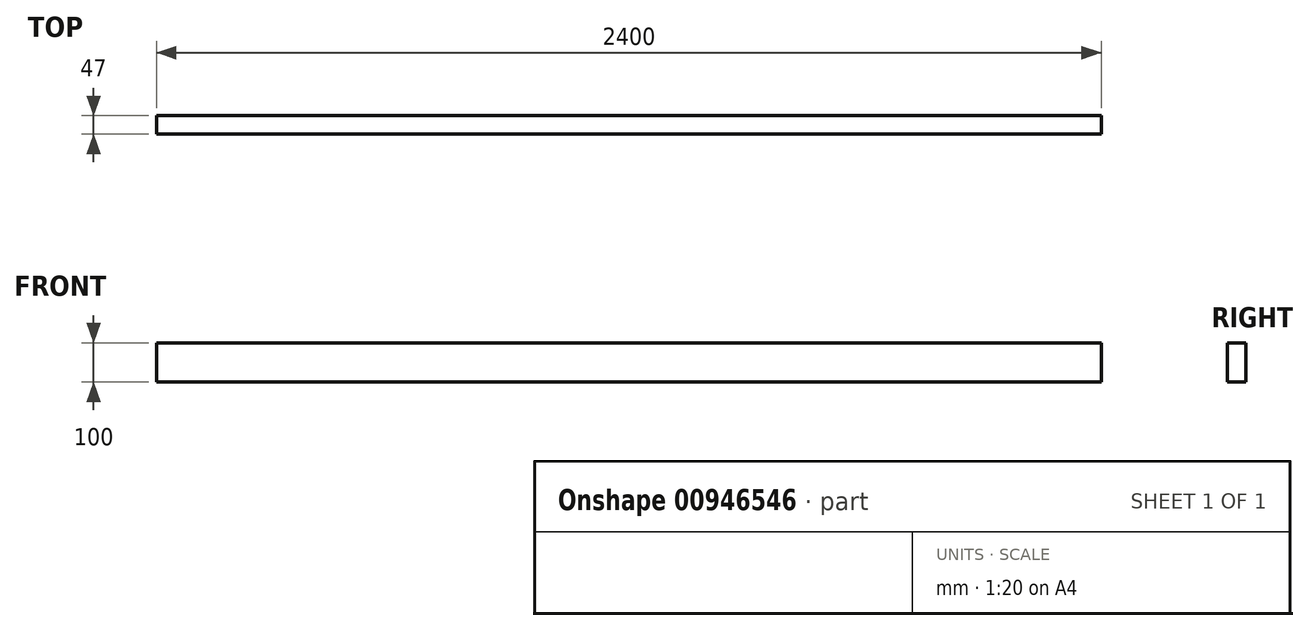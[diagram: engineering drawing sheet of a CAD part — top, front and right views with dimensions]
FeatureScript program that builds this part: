
annotation { "Feature Type Name" : "Feature", "Feature Type Description" : "" }
export const myFeature = defineFeature(function(context is Context, id is Id, definition is map)
    precondition{}
    {
        {
            var Q0;
            Q0=qCreatedBy(makeId("Right.planeOp"),FACE);
            var sketch = newSketch(context, id + "F0", { "sketchPlane" : qUnion([Q0])});
            skLineSegment(sketch, "E0.bottom", {"start": v(0, 0) * mm, "end": v(-47, 0) * mm});
            skLineSegment(sketch, "E0.top", {"start": v(0, 100) * mm, "end": v(-47, 100) * mm});
            skLineSegment(sketch, "E0.left", {"start": v(0, 0) * mm, "end": v(0, 100) * mm});
            skLineSegment(sketch, "E0.right", {"start": v(-47, 0) * mm, "end": v(-47, 100) * mm});
            skSolve(sketch);
        }
        {
            var Q0;
            Q0=qSketchRegion(id+"F0",true);
            extrude(context, id + "F1", {"entities" : qUnion([Q0]), "depth" : 2400 * mm, "offsetDistance" : 25 * mm});
        }
    });
